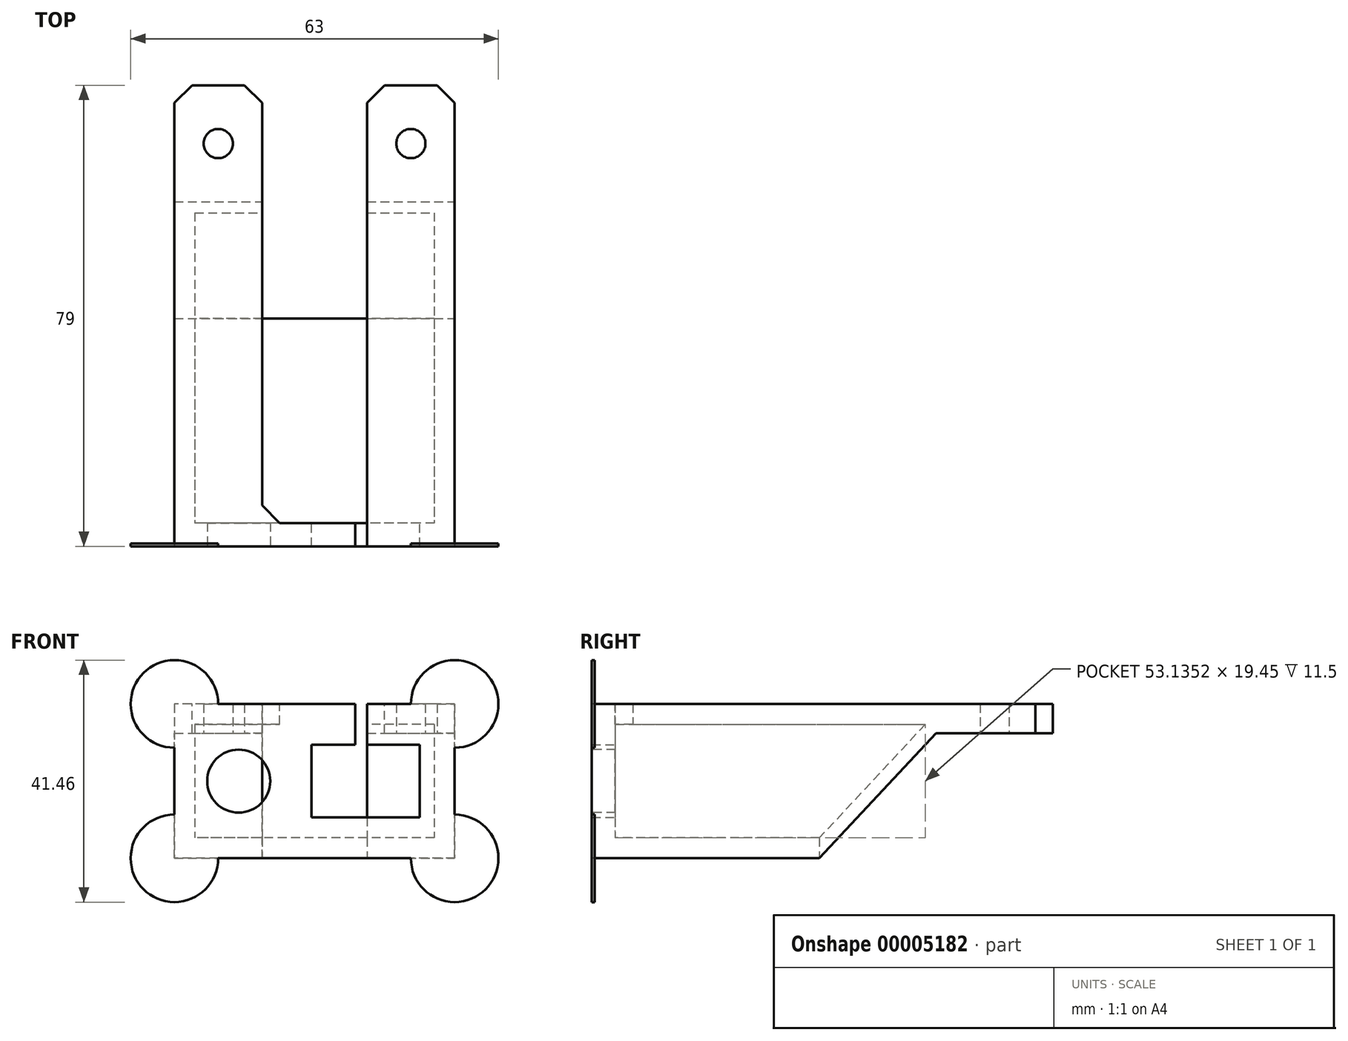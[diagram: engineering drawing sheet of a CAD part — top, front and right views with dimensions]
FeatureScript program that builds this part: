
annotation { "Feature Type Name" : "Feature", "Feature Type Description" : "" }
export const myFeature = defineFeature(function(context is Context, id is Id, definition is map)
    precondition{}
    {
        {
            var Q0;
            Q0=qCreatedBy(makeId("Front.planeOp"),FACE);
            var sketch = newSketch(context, id + "F0", { "sketchPlane" : qUnion([Q0])});
            skCircle(sketch, "E0", {"center": v(0, 0) * mm, "radius": 5 * mm});
            skLineSegment(sketch, "E1", {"start": v(0, 0) * mm, "end": v(21.75, 0) * mm, "construction": true});
            skLineSegment(sketch, "E2.bottom", {"start": v(31, 6.22) * mm, "end": v(12.5, 6.22) * mm});
            skLineSegment(sketch, "E2.top", {"start": v(31, -6.22) * mm, "end": v(12.5, -6.22) * mm});
            skLineSegment(sketch, "E2.left", {"start": v(31, 6.22) * mm, "end": v(31, -6.23) * mm});
            skLineSegment(sketch, "E2.right", {"start": v(12.5, 6.22) * mm, "end": v(12.5, -6.23) * mm});
            skPoint(sketch, "E2.middle", {"position": v(21.75, 0) * mm});
            skLineSegment(sketch, "E3.bottom", {"start": v(37, 13.22) * mm, "end": v(-11, 13.22) * mm});
            skLineSegment(sketch, "E3.top", {"start": v(37, -13.22) * mm, "end": v(-11, -13.22) * mm});
            skLineSegment(sketch, "E3.left", {"start": v(37, 13.22) * mm, "end": v(37, -13.22) * mm});
            skLineSegment(sketch, "E3.right", {"start": v(-11, 13.22) * mm, "end": v(-11, -13.22) * mm});
            skPoint(sketch, "E3.middle", {"position": v(13, 0) * mm});
            skSolve(sketch);
        }
        {
            var Q0;
            Q0 = qSketchRegion(id + "F0", true);
            extrude(context, id + "F1", {"entities" : qUnion([Q0]), "depth" : 4 * mm, "offsetDistance" : 25 * mm});
        }
        {
            var Q0;
            Q0=makeQuery(id+"F1.opExtrude","CAP_FACE",FACE,{"disambiguationData":[OSD([sQuery(id+"F0.wireOp",EDGE,"E0"),sQuery(id+"F0.wireOp",EDGE,"E2.bottom"),sQuery(id+"F0.wireOp",EDGE,"E2.top"),sQuery(id+"F0.wireOp",EDGE,"E2.left"),sQuery(id+"F0.wireOp",EDGE,"E2.right"),sQuery(id+"F0.wireOp",EDGE,"E3.bottom"),sQuery(id+"F0.wireOp",EDGE,"E3.top"),sQuery(id+"F0.wireOp",EDGE,"E3.left"),sQuery(id+"F0.wireOp",EDGE,"E3.right")])],"isStart":true});
            var sketch = newSketch(context, id + "F2", { "sketchPlane" : qUnion([Q0])});
            skLineSegment(sketch, "E4", {"start": v(-37, 13.23) * mm, "end": v(11, -13.22) * mm, "construction": true});
            skLineSegment(sketch, "E5.0", {"start": v(-37, 13.22) * mm, "end": v(11, 13.22) * mm});
            skLineSegment(sketch, "E5.1", {"start": v(-37, 13.22) * mm, "end": v(-37, -13.22) * mm});
            skLineSegment(sketch, "E5.2", {"start": v(-37, -13.22) * mm, "end": v(11, -13.22) * mm});
            skLineSegment(sketch, "E5.3", {"start": v(11, 13.22) * mm, "end": v(11, -13.22) * mm});
            skLineSegment(sketch, "E6.0", {"start": v(-33.5, 9.72) * mm, "end": v(7.5, 9.72) * mm});
            skLineSegment(sketch, "E6.1", {"start": v(-33.5, 9.72) * mm, "end": v(-33.5, -9.72) * mm});
            skLineSegment(sketch, "E6.2", {"start": v(-33.5, -9.72) * mm, "end": v(7.5, -9.72) * mm});
            skLineSegment(sketch, "E6.3", {"start": v(7.5, 9.72) * mm, "end": v(7.5, -9.72) * mm});
            skSolve(sketch);
        }
        {
            var Q0;
            Q0 = qSketchRegion(id + "F2", true);
            extrude(context, id + "F3", {"entities" : qUnion([Q0]), "operationType" : NewBodyOperationType.ADD, "depth" : 35 * mm, "offsetDistance" : 25 * mm});
        }
        {
            var Q0;
            Q0=makeQuery(id+"F3.opExtrude","CAP_FACE",FACE,{"disambiguationData":[OSD([sQuery(id+"F2.wireOp",EDGE,"E5.0"),sQuery(id+"F2.wireOp",EDGE,"E5.1"),sQuery(id+"F2.wireOp",EDGE,"E5.2"),sQuery(id+"F2.wireOp",EDGE,"E5.3"),sQuery(id+"F2.wireOp",EDGE,"E6.0"),sQuery(id+"F2.wireOp",EDGE,"E6.1"),sQuery(id+"F2.wireOp",EDGE,"E6.2"),sQuery(id+"F2.wireOp",EDGE,"E6.3")])],"isStart":false});
            var sketch = newSketch(context, id + "F4", { "sketchPlane" : qUnion([Q0])});
            skLineSegment(sketch, "E7", {"start": v(-13, 13.22) * mm, "end": v(-13, 9.72) * mm, "construction": true});
            skLineSegment(sketch, "E8.bottom", {"start": v(-4, 13.22) * mm, "end": v(-22, 13.22) * mm});
            skLineSegment(sketch, "E8.top", {"start": v(-4, 9.72) * mm, "end": v(-22, 9.72) * mm});
            skLineSegment(sketch, "E8.left", {"start": v(-4, 13.22) * mm, "end": v(-4, 9.72) * mm});
            skLineSegment(sketch, "E8.right", {"start": v(-22, 13.22) * mm, "end": v(-22, 9.72) * mm});
            skPoint(sketch, "E8.middle", {"position": v(-13, 11.47) * mm});
            skSolve(sketch);
        }
        {
            var Q0;
            Q0 = qSketchRegion(id + "F4", true);
            var Q1;
            Q1=makeQuery(id+"F1.opExtrude","CAP_FACE",FACE,{"disambiguationData":[OSD([sQuery(id+"F0.wireOp",EDGE,"E0"),sQuery(id+"F0.wireOp",EDGE,"E2.bottom"),sQuery(id+"F0.wireOp",EDGE,"E2.top"),sQuery(id+"F0.wireOp",EDGE,"E2.left"),sQuery(id+"F0.wireOp",EDGE,"E2.right"),sQuery(id+"F0.wireOp",EDGE,"E3.bottom"),sQuery(id+"F0.wireOp",EDGE,"E3.top"),sQuery(id+"F0.wireOp",EDGE,"E3.left"),sQuery(id+"F0.wireOp",EDGE,"E3.right")])],"isStart":true});
            extrude(context, id + "F5", {"entities" : qUnion([Q0]), "operationType" : NewBodyOperationType.REMOVE, "endBound" : BoundingType.UP_TO_SURFACE, "oppositeDirection" : true, "depth" : 25 * mm, "endBoundEntityFace" : qUnion([Q1]), "offsetDistance" : 25 * mm});
        }
        {
            var Q0;
            Q0=makeQuery(id+"F5.boolean.opBoolean","MERGE",FACE,{"derivedFrom":[makeQuery(id+"F1.opExtrude","CAP_FACE",FACE,{"disambiguationData":[OSD([sQuery(id+"F0.wireOp",EDGE,"E0"),sQuery(id+"F0.wireOp",EDGE,"E2.bottom"),sQuery(id+"F0.wireOp",EDGE,"E2.top"),sQuery(id+"F0.wireOp",EDGE,"E2.left"),sQuery(id+"F0.wireOp",EDGE,"E2.right"),sQuery(id+"F0.wireOp",EDGE,"E3.bottom"),sQuery(id+"F0.wireOp",EDGE,"E3.top"),sQuery(id+"F0.wireOp",EDGE,"E3.left"),sQuery(id+"F0.wireOp",EDGE,"E3.right")])],"isStart":true})],"fromTools":[makeQuery(id+"F5.opExtrude","CAP_FACE",FACE,{"disambiguationData":[OSD([sQuery(id+"F4.wireOp",EDGE,"E8.bottom"),sQuery(id+"F4.wireOp",EDGE,"E8.top"),sQuery(id+"F4.wireOp",EDGE,"E8.left"),sQuery(id+"F4.wireOp",EDGE,"E8.right")])],"isStart":false})]});
            var sketch = newSketch(context, id + "F6", { "sketchPlane" : qUnion([Q0])});
            skLineSegment(sketch, "E9.bottom", {"start": v(-22, 13.22) * mm, "end": v(-20, 13.22) * mm});
            skLineSegment(sketch, "E9.top", {"start": v(-22, 6.22) * mm, "end": v(-20, 6.22) * mm});
            skLineSegment(sketch, "E9.left", {"start": v(-22, 13.22) * mm, "end": v(-22, 6.22) * mm});
            skLineSegment(sketch, "E9.right", {"start": v(-20, 13.22) * mm, "end": v(-20, 6.22) * mm});
            skSolve(sketch);
        }
        {
            var Q0;
            Q0 = qSketchRegion(id + "F6", true);
            extrude(context, id + "F7", {"entities" : qUnion([Q0]), "operationType" : NewBodyOperationType.REMOVE, "endBound" : BoundingType.THROUGH_ALL, "oppositeDirection" : true, "depth" : 25 * mm, "offsetDistance" : 25 * mm});
        }
        {
            var Q0;
            Q0=makeQuery(id+"F3.opExtrude","CAP_FACE",FACE,{"disambiguationData":[OSD([sQuery(id+"F2.wireOp",EDGE,"E5.0"),sQuery(id+"F2.wireOp",EDGE,"E5.1"),sQuery(id+"F2.wireOp",EDGE,"E5.2"),sQuery(id+"F2.wireOp",EDGE,"E5.3"),sQuery(id+"F2.wireOp",EDGE,"E6.0"),sQuery(id+"F2.wireOp",EDGE,"E6.1"),sQuery(id+"F2.wireOp",EDGE,"E6.2"),sQuery(id+"F2.wireOp",EDGE,"E6.3")])],"isStart":false});
            var sketch = newSketch(context, id + "F8", { "sketchPlane" : qUnion([Q0])});
            skLineSegment(sketch, "E10.bottom", {"start": v(-37, 13.22) * mm, "end": v(-22, 13.22) * mm});
            skLineSegment(sketch, "E10.top", {"start": v(-37, -13.22) * mm, "end": v(-22, -13.22) * mm});
            skLineSegment(sketch, "E10.left", {"start": v(-37, 13.22) * mm, "end": v(-37, -13.22) * mm});
            skLineSegment(sketch, "E10.right", {"start": v(-22, 13.22) * mm, "end": v(-22, -13.22) * mm});
            skLineSegment(sketch, "E11.bottom", {"start": v(11, 13.22) * mm, "end": v(-4, 13.22) * mm});
            skLineSegment(sketch, "E11.top", {"start": v(11, -13.22) * mm, "end": v(-4, -13.22) * mm});
            skLineSegment(sketch, "E11.left", {"start": v(11, 13.22) * mm, "end": v(11, -13.22) * mm});
            skLineSegment(sketch, "E11.right", {"start": v(-4, 13.22) * mm, "end": v(-4, -13.22) * mm});
            skSolve(sketch);
        }
        {
            var Q0;
            Q0 = qSketchRegion(id + "F8", true);
            extrude(context, id + "F9", {"entities" : qUnion([Q0]), "operationType" : NewBodyOperationType.ADD, "depth" : 40 * mm, "offsetDistance" : 25 * mm});
        }
        {
            var Q0;
            Q0=makeQuery(id+"F9.boolean.opBoolean","MERGE",FACE,{"derivedFrom":[makeQuery(id+"F3.boolean.opBoolean","MERGE",FACE,{"derivedFrom":[makeQuery(id+"F1.opExtrude","SWEPT_FACE",FACE,{"disambiguationData":[OSD([sQuery(id+"F0.wireOp",EDGE,"E3.left")])]}),makeQuery(id+"F3.opExtrude","SWEPT_FACE",FACE,{"disambiguationData":[OSD([sQuery(id+"F2.wireOp",EDGE,"E5.1")])]})]}),makeQuery(id+"F9.opExtrude","SWEPT_FACE",FACE,{"disambiguationData":[OSD([sQuery(id+"F8.wireOp",EDGE,"E10.left")])]})]});
            var sketch = newSketch(context, id + "F10", { "sketchPlane" : qUnion([Q0])});
            skLineSegment(sketch, "E12.0", {"start": v(35, -9.72) * mm, "end": v(35, -13.22) * mm, "construction": true});
            skLineSegment(sketch, "E13", {"start": v(35, -13.22) * mm, "end": v(55, 8.22) * mm});
            skLineSegment(sketch, "E14", {"start": v(55, 8.22) * mm, "end": v(75, 8.23) * mm});
            skLineSegment(sketch, "E15", {"start": v(75, 8.22) * mm, "end": v(75, -13.22) * mm});
            skLineSegment(sketch, "E16", {"start": v(75, -13.22) * mm, "end": v(35, -13.23) * mm});
            skSolve(sketch);
        }
        {
            var Q0;
            Q0 = qSketchRegion(id + "F10", true);
            extrude(context, id + "F11", {"entities" : qUnion([Q0]), "operationType" : NewBodyOperationType.REMOVE, "endBound" : BoundingType.THROUGH_ALL, "oppositeDirection" : true, "depth" : 25 * mm, "offsetDistance" : 25 * mm});
        }
        {
            var Q0;
            Q0=makeQuery(id+"F11.boolean.opBoolean","COPY",FACE,{"disambiguationData":[TD([makeQuery(id+"F1.opExtrude","SWEPT_FACE",FACE,{"disambiguationData":[OSD([sQuery(id+"F0.wireOp",EDGE,"E3.left")])]})])],"derivedFrom":makeQuery(id+"F11.opExtrude","SWEPT_FACE",FACE,{"disambiguationData":[OSD([sQuery(id+"F10.wireOp",EDGE,"E14")])]})});
            var sketch = newSketch(context, id + "F12", { "sketchPlane" : qUnion([Q0])});
            skLineSegment(sketch, "E17", {"start": v(37, -55) * mm, "end": v(22, -75) * mm, "construction": true});
            skCircle(sketch, "E18", {"center": v(29.5, -65) * mm, "radius": 2.5 * mm});
            skSolve(sketch);
        }
        {
            var Q0;
            Q0 = qSketchRegion(id + "F12", true);
            extrude(context, id + "F13", {"entities" : qUnion([Q0]), "operationType" : NewBodyOperationType.REMOVE, "endBound" : BoundingType.THROUGH_ALL, "oppositeDirection" : true, "depth" : 25 * mm, "offsetDistance" : 25 * mm});
        }
        {
            var Q0;
            Q0=makeQuery(id+"F11.boolean.opBoolean","COPY",FACE,{"disambiguationData":[TD([makeQuery(id+"F1.opExtrude","SWEPT_FACE",FACE,{"disambiguationData":[OSD([sQuery(id+"F0.wireOp",EDGE,"E3.right")])]})])],"derivedFrom":makeQuery(id+"F11.opExtrude","SWEPT_FACE",FACE,{"disambiguationData":[OSD([sQuery(id+"F10.wireOp",EDGE,"E14")])]})});
            var sketch = newSketch(context, id + "F14", { "sketchPlane" : qUnion([Q0])});
            skLineSegment(sketch, "E19", {"start": v(-11, -75) * mm, "end": v(4, -55) * mm, "construction": true});
            skCircle(sketch, "E20", {"center": v(-3.5, -65) * mm, "radius": 2.5 * mm});
            skSolve(sketch);
        }
        {
            var Q0;
            Q0 = qSketchRegion(id + "F14", true);
            extrude(context, id + "F15", {"entities" : qUnion([Q0]), "operationType" : NewBodyOperationType.REMOVE, "endBound" : BoundingType.THROUGH_ALL, "oppositeDirection" : true, "depth" : 25 * mm, "offsetDistance" : 25 * mm});
        }
        {
            var Q0;
            Q0=makeQuery(id+"F9.boolean.opBoolean","MERGE",FACE,{"derivedFrom":[makeQuery(id+"F5.boolean.opBoolean","COPY",FACE,{"derivedFrom":makeQuery(id+"F5.opExtrude","SWEPT_FACE",FACE,{"disambiguationData":[OSD([sQuery(id+"F4.wireOp",EDGE,"E8.left")])]})}),makeQuery(id+"F9.opExtrude","SWEPT_FACE",FACE,{"disambiguationData":[OSD([sQuery(id+"F8.wireOp",EDGE,"E11.right")])]})]});
            var sketch = newSketch(context, id + "F16", { "sketchPlane" : qUnion([Q0])});
            skLineSegment(sketch, "E21", {"start": v(35, 9.72) * mm, "end": v(53.14, 9.73) * mm});
            skLineSegment(sketch, "E22", {"start": v(53.14, 9.73) * mm, "end": v(35, -9.73) * mm});
            skLineSegment(sketch, "E23", {"start": v(35, -9.72) * mm, "end": v(35, 9.72) * mm});
            skSolve(sketch);
        }
        {
            var Q0;
            Q0 = qSketchRegion(id + "F16", true);
            var Q1;
            Q1=makeQuery(id+"F3.opExtrude","SWEPT_FACE",FACE,{"disambiguationData":[OSD([sQuery(id+"F2.wireOp",EDGE,"E6.3")])]});
            var Q2;
            Q2=makeQuery(id+"F3.opExtrude","SWEPT_FACE",FACE,{"disambiguationData":[OSD([sQuery(id+"F2.wireOp",EDGE,"E6.1")])]});
            extrude(context, id + "F17", {"entities" : qUnion([Q0]), "operationType" : NewBodyOperationType.REMOVE, "endBound" : BoundingType.UP_TO_SURFACE, "oppositeDirection" : true, "depth" : 25 * mm, "endBoundEntityFace" : qUnion([Q1]), "offsetDistance" : 25 * mm, "hasSecondDirection" : true, "secondDirectionBound" : BoundingType.UP_TO_SURFACE, "secondDirectionOppositeDirection" : false, "secondDirectionDepth" : 25 * mm, "secondDirectionBoundEntityFace" : qUnion([Q2])});
        }
        {
            var Q0;
            {var subQ0=sQuery(id+"F16.wireOp",EDGE,"E22");var subQ1=sQuery(id+"F16.wireOp",EDGE,"E21");Q0=makeQuery(id+"F17.boolean.opBoolean","COPY",EDGE,{"disambiguationData":[TD([makeQuery(id+"F3.opExtrude","SWEPT_FACE",FACE,{"disambiguationData":[OSD([sQuery(id+"F2.wireOp",EDGE,"E6.3")])]})])],"derivedFrom":makeQuery(id+"F17.opExtrude","TWEAK_EDGE",EDGE,{"derivedFrom":[makeQuery(id+"F16.imprint","IMPRINT",EDGE,{"derivedFrom":subQ1}),makeQuery(id+"F16.imprint","IMPRINT",EDGE,{"derivedFrom":subQ0})]})});}
            var Q1;
            {var subQ0=sQuery(id+"F16.wireOp",EDGE,"E21");var subQ1=sQuery(id+"F16.wireOp",EDGE,"E22");Q1=makeQuery(id+"F17.boolean.opBoolean","COPY",EDGE,{"disambiguationData":[TD([makeQuery(id+"F3.opExtrude","SWEPT_FACE",FACE,{"disambiguationData":[OSD([sQuery(id+"F2.wireOp",EDGE,"E6.1")])]})])],"derivedFrom":makeQuery(id+"F17.opExtrude","TWEAK_EDGE",EDGE,{"derivedFrom":[makeQuery(id+"F16.imprint","IMPRINT",EDGE,{"derivedFrom":subQ0}),makeQuery(id+"F16.imprint","IMPRINT",EDGE,{"derivedFrom":subQ1})]})});}
            var Q2;
            Q2=makeQuery(id+"F7.boolean.opBoolean","COPY",EDGE,{"derivedFrom":makeQuery(id+"F7.opExtrude","SWEPT_EDGE",EDGE,{"disambiguationData":[OSD([sQuery(id+"F0.wireOp",EDGE,"E0"),sQuery(id+"F0.wireOp",EDGE,"E2.bottom"),sQuery(id+"F0.wireOp",EDGE,"E2.top"),sQuery(id+"F0.wireOp",EDGE,"E2.left"),sQuery(id+"F0.wireOp",EDGE,"E2.right"),sQuery(id+"F0.wireOp",EDGE,"E3.bottom"),sQuery(id+"F0.wireOp",EDGE,"E3.top"),sQuery(id+"F0.wireOp",EDGE,"E3.left"),sQuery(id+"F0.wireOp",EDGE,"E3.right"),sQuery(id+"F4.wireOp",EDGE,"E8.bottom"),sQuery(id+"F6.wireOp",EDGE,"E9.bottom"),sQuery(id+"F6.wireOp",EDGE,"E9.right")])]})});
            var Q3;
            Q3=makeQuery(id+"F7.boolean.opBoolean","COPY",EDGE,{"derivedFrom":makeQuery(id+"F7.opExtrude","SWEPT_EDGE",EDGE,{"disambiguationData":[OSD([sQuery(id+"F0.wireOp",EDGE,"E2.bottom"),sQuery(id+"F6.wireOp",EDGE,"E9.top"),sQuery(id+"F6.wireOp",EDGE,"E9.right")])]})});
            var Q4;
            Q4=makeQuery(id+"F7.boolean.opBoolean","COPY",EDGE,{"derivedFrom":makeQuery(id+"F7.opExtrude","SWEPT_EDGE",EDGE,{"disambiguationData":[OSD([sQuery(id+"F0.wireOp",EDGE,"E2.bottom"),sQuery(id+"F6.wireOp",EDGE,"E9.top"),sQuery(id+"F6.wireOp",EDGE,"E9.left")])]})});
            var Q5;
            Q5=makeQuery(id+"F5.boolean.opBoolean","COPY",EDGE,{"derivedFrom":makeQuery(id+"F5.opExtrude","CAP_EDGE",EDGE,{"disambiguationData":[OSD([sQuery(id+"F4.wireOp",EDGE,"E8.left")])],"isStart":false})});
            var Q6;
            Q6=makeQuery(id+"F9.opExtrude","CAP_EDGE",EDGE,{"disambiguationData":[OSD([sQuery(id+"F8.wireOp",EDGE,"E10.left")])],"isStart":false});
            var Q7;
            Q7=makeQuery(id+"F9.opExtrude","CAP_EDGE",EDGE,{"disambiguationData":[OSD([sQuery(id+"F8.wireOp",EDGE,"E10.right")])],"isStart":false});
            var Q8;
            Q8=makeQuery(id+"F9.opExtrude","CAP_EDGE",EDGE,{"disambiguationData":[OSD([sQuery(id+"F8.wireOp",EDGE,"E11.right")])],"isStart":false});
            var Q9;
            Q9=makeQuery(id+"F9.opExtrude","CAP_EDGE",EDGE,{"disambiguationData":[OSD([sQuery(id+"F8.wireOp",EDGE,"E11.left")])],"isStart":false});
            chamfer(context, id + "F18", {"entities" : qUnion([Q0, Q1, Q2, Q3, Q4, Q5, Q6, Q7, Q8, Q9]), "width" : 3 * mm, "tangentPropagation" : true});
        }
        {
            var Q0;
            Q0=makeQuery(id+"F1.opExtrude","CAP_FACE",FACE,{"disambiguationData":[OSD([sQuery(id+"F0.wireOp",EDGE,"E0"),sQuery(id+"F0.wireOp",EDGE,"E2.bottom"),sQuery(id+"F0.wireOp",EDGE,"E2.top"),sQuery(id+"F0.wireOp",EDGE,"E2.left"),sQuery(id+"F0.wireOp",EDGE,"E2.right"),sQuery(id+"F0.wireOp",EDGE,"E3.bottom"),sQuery(id+"F0.wireOp",EDGE,"E3.top"),sQuery(id+"F0.wireOp",EDGE,"E3.left"),sQuery(id+"F0.wireOp",EDGE,"E3.right")])],"isStart":false});
            var sketch = newSketch(context, id + "F19", { "sketchPlane" : qUnion([Q0])});
            skCircle(sketch, "E24", {"center": v(-11, 13.22) * mm, "radius": 7.5 * mm});
            skCircle(sketch, "E25", {"center": v(37, 13.22) * mm, "radius": 7.5 * mm});
            skCircle(sketch, "E26", {"center": v(37, -13.22) * mm, "radius": 7.5 * mm});
            skCircle(sketch, "E27", {"center": v(-11, -13.22) * mm, "radius": 7.5 * mm});
            skSolve(sketch);
        }
        {
            var Q0;
            Q0 = qSketchRegion(id + "F19", true);
            extrude(context, id + "F20", {"entities" : qUnion([Q0]), "operationType" : NewBodyOperationType.ADD, "oppositeDirection" : true, "depth" : 0.5 * mm, "offsetDistance" : 25 * mm});
        }
        {
            var Q0;
            Q0=makeQuery(id+"F20.boolean.opBoolean","MERGE",FACE,{"derivedFrom":[makeQuery(id+"F1.opExtrude","CAP_FACE",FACE,{"disambiguationData":[OSD([sQuery(id+"F0.wireOp",EDGE,"E0"),sQuery(id+"F0.wireOp",EDGE,"E2.bottom"),sQuery(id+"F0.wireOp",EDGE,"E2.top"),sQuery(id+"F0.wireOp",EDGE,"E2.left"),sQuery(id+"F0.wireOp",EDGE,"E2.right"),sQuery(id+"F0.wireOp",EDGE,"E3.bottom"),sQuery(id+"F0.wireOp",EDGE,"E3.top"),sQuery(id+"F0.wireOp",EDGE,"E3.left"),sQuery(id+"F0.wireOp",EDGE,"E3.right")])],"isStart":false}),makeQuery(id+"F20.opExtrude","CAP_FACE",FACE,{"disambiguationData":[OSD([sQuery(id+"F19.wireOp",EDGE,"E24")])],"isStart":true}),makeQuery(id+"F20.opExtrude","CAP_FACE",FACE,{"disambiguationData":[OSD([sQuery(id+"F19.wireOp",EDGE,"E25")])],"isStart":true}),makeQuery(id+"F20.opExtrude","CAP_FACE",FACE,{"disambiguationData":[OSD([sQuery(id+"F19.wireOp",EDGE,"E26")])],"isStart":true}),makeQuery(id+"F20.opExtrude","CAP_FACE",FACE,{"disambiguationData":[OSD([sQuery(id+"F19.wireOp",EDGE,"E27")])],"isStart":true})]});
            var sketch = newSketch(context, id + "F21", { "sketchPlane" : qUnion([Q0])});
            skCircle(sketch, "E28", {"center": v(0, 0) * mm, "radius": 5.4 * mm});
            skSolve(sketch);
        }
        {
            var Q0;
            Q0 = qSketchRegion(id + "F21", true);
            var Q1;
            Q1=makeQuery(id+"F5.boolean.opBoolean","MERGE",FACE,{"derivedFrom":[makeQuery(id+"F1.opExtrude","CAP_FACE",FACE,{"disambiguationData":[OSD([sQuery(id+"F0.wireOp",EDGE,"E0"),sQuery(id+"F0.wireOp",EDGE,"E2.bottom"),sQuery(id+"F0.wireOp",EDGE,"E2.top"),sQuery(id+"F0.wireOp",EDGE,"E2.left"),sQuery(id+"F0.wireOp",EDGE,"E2.right"),sQuery(id+"F0.wireOp",EDGE,"E3.bottom"),sQuery(id+"F0.wireOp",EDGE,"E3.top"),sQuery(id+"F0.wireOp",EDGE,"E3.left"),sQuery(id+"F0.wireOp",EDGE,"E3.right")])],"isStart":true})],"fromTools":[makeQuery(id+"F5.opExtrude","CAP_FACE",FACE,{"disambiguationData":[OSD([sQuery(id+"F4.wireOp",EDGE,"E8.bottom"),sQuery(id+"F4.wireOp",EDGE,"E8.top"),sQuery(id+"F4.wireOp",EDGE,"E8.left"),sQuery(id+"F4.wireOp",EDGE,"E8.right")])],"isStart":false})]});
            extrude(context, id + "F22", {"entities" : qUnion([Q0]), "operationType" : NewBodyOperationType.REMOVE, "endBound" : BoundingType.UP_TO_SURFACE, "oppositeDirection" : true, "depth" : 25 * mm, "endBoundEntityFace" : qUnion([Q1]), "offsetDistance" : 25 * mm});
        }
    });
